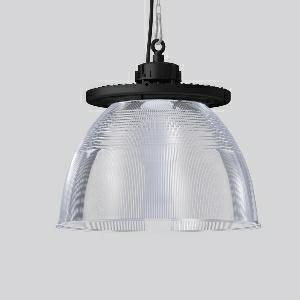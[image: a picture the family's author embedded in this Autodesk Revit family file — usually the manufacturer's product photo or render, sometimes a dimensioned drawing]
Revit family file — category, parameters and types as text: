
# Revit family: industrial_hall_refraktor_921709_003_2f2d
name_source: partatom
category: Lighting Fixtures
units: mm (PartAtom-declared; Revit-internal decimal feet)

## family parameters
Cut with Voids When Loaded = No
Host = Face
Light Source = No
Part Type = Normal
Room Calculation Point = No
Round Connector Dimension = Use Diameter
Shared = No

## types (1)
- INDUSTRIAL HALL refraktor (1 x LED Modul 840, 33300 lm, 4000)
    Apparent Load = 220 VA
    CIE Flux Codes = 84 94 98 93 100
    Color Rendering = 80
    Color Temperature = 4000
    Default Elevation = 1800 mm
    Description = Series: INDUSTRIAL HALL
Round highbay luminaire for chain or cable suspension. Robust housing made of die-cast aluminium with eye ring, powder coated. Vertical cooling ribs ensure constant heat dissipation for optimal thermal management. Diffuser made of clear, non-reflecting, single pane safety glass (toughened glass). Refractor: PMMA, transparent. Primary light control with high-performance wide-area LEDs and reflector made of plastic (PMMA) for optimum glare limitation: RUG <19. Easy to install thanks to 1-point suspension. Suitable for chain or steel cable suspension (to be provided on site). With power cord (1.5 m). Ceiling- and wall-mounting bracket available as accessory. Luminaire with limited surface temperature in accordance with EN 60598-2-24 for use in environments in which a deposit of conductive dust on the luminaire can be expected. Qualified for use in the food and drink industry. 
Colour: deep black, matt (RAL 9005)
Diameter: 570 mm
Height: 521 mm
Lamp: LED
Socket: without socket
Colour temperature: 4000K
Colour rendering index (CRI): 80
System power: 220 W
Rated luminous flux: 33300 lm
Luminous efficiency: 151 lm/W
Control gear: Regulated power supply
Protection class: I
Type of protection: IP 65
    Height = 521 mm
    Lamp = 1 x LED Modul 840
    Lamp Light Flux = 33300 lm
    Lamp count = 1
    Length = 570 mm
    Lifetime = 50000 h
    Luminous efficacy = 151 lm/W
    Manufacturer = RZB
    ModVariant = No
    Model = 921709.003
    Mounting Place = Ceiling
    Mounting Type = Pendant
    Number of Poles = 1
    OnlyDefault = Yes
    Power Factor = 1
    Product Name = INDUSTRIAL HALL refraktor
    Product group = Pendant commercial luminaires
    ProductGroupID = 903
    Protection Class = Protection class I
    Protection Degree = Degree of protection
    RLX_Detail_Level = 1
    RLX_Emergency_Light_Flux = 0 lm
    RLX_Emergency_Type = 0
    RLX_Emergency_Type_DB = No
    RlxData = <blob elided: 254537 chars, md5=8b7cfcf4>
    Socket = socket
    Standby Power = 0 W
    System Light Flux = 33299 lm
    System Power = 220 W
    Type Comments = Product without accessories
    Type Image = 921709.003.jpg
    URL = http://relux.com
    VarID = ---
    Voltage = 0 V
    Weight = 0.00 kg
    Width = 0 mm  [stored 0 ft]

note: [stored X ft] marks values corroborated as IEEE doubles in the binary element streams (Revit-internal decimal feet)

## geometry (parser evidence)
native form markers: Blend x4, Sweep x13
no freeform markers — native parametric forms only
